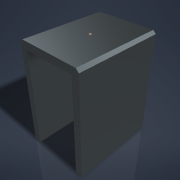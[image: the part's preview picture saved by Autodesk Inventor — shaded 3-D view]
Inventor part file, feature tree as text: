
AUTODESK INVENTOR PART (.ipt)
format: ipt  version: 2022 (Build 260153070, 153G)  size: 175,616 bytes
history: native  units: mm
features: hole x7, sketch x6, other x4, extrude x2, chamfer x1
ambient origin geometry x8: Origin, YZ Plane, XZ Plane, XY Plane, X Axis, Y Axis, Z Axis, Center Point
bodies: Body1 (feature_tree)
feature tree (20):
  sketch  "Эскиз1"
  extrude  "Выдавливание3"  Depth=46.0mm
  extrude  "Выдавливание4"  Depth=36.0mm
  other  "РабПлоскость5"
  other  "РабТочка2"
  other  "РабОсь2"
  sketch  "Эскиз3"
  hole  "Отверстие3"  [1 undecoded]
  hole  "Отверстие4"  [1 undecoded]
  hole  "Отверстие5"  [1 undecoded]
  sketch  "Эскиз9"
  hole  "Отверстие7"  [1 undecoded]
  sketch  "Эскиз8"
  hole  "Отверстие9"  [1 undecoded]
  hole  "Отверстие10"  [1 undecoded]
  hole  "Отверстие11"  [1 undecoded]
  chamfer  "Фаска1"  Distance=15.0mm
  sketch  "Эскиз4"
  sketch  "Эскиз5"
  other  "Проецирование ребер1"
note: 7 required parameter values undecoded (feature->parameter linkage not recoverable at this tier; creation-order binding heuristic only, values carry confidence <= 0.55)
